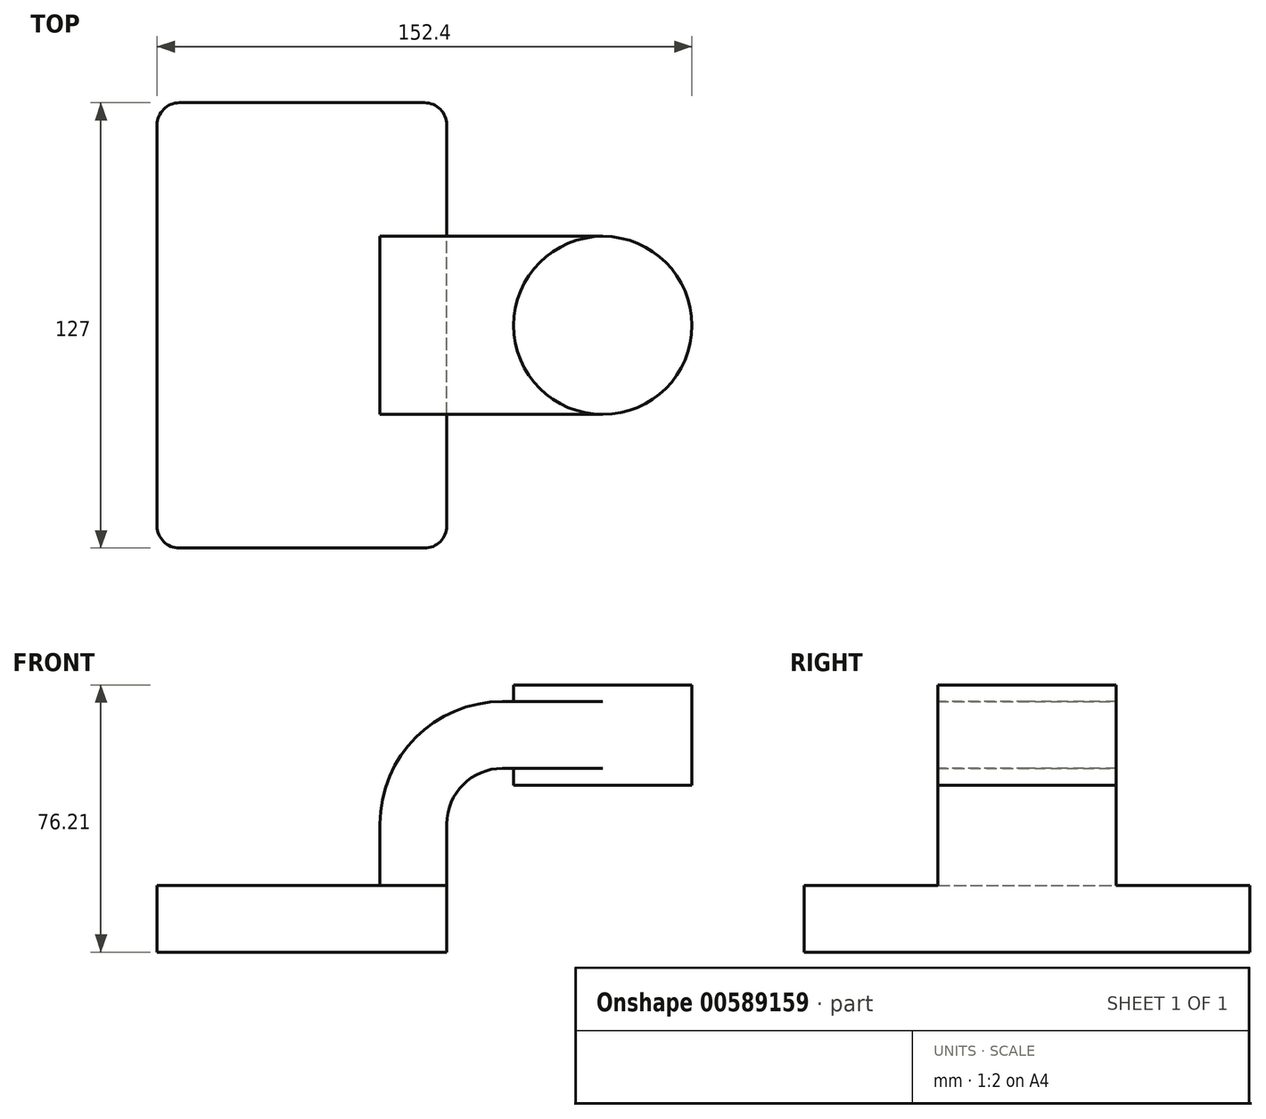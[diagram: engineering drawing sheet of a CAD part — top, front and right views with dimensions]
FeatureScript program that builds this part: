
annotation { "Feature Type Name" : "Feature", "Feature Type Description" : "" }
export const myFeature = defineFeature(function(context is Context, id is Id, definition is map)
    precondition{}
    {
        {
            var Q0;
            Q0=qCreatedBy(makeId("Front.planeOp"),FACE);
            var sketch = newSketch(context, id + "F0", { "sketchPlane" : qUnion([Q0])});
            skLineSegment(sketch, "E0.bottom", {"start": v(-41.28, -9.53) * mm, "end": v(41.28, -9.53) * mm});
            skLineSegment(sketch, "E0.top", {"start": v(-41.28, 9.53) * mm, "end": v(41.28, 9.53) * mm});
            skLineSegment(sketch, "E0.left", {"start": v(-41.28, -9.53) * mm, "end": v(-41.28, 9.53) * mm});
            skLineSegment(sketch, "E0.right", {"start": v(41.28, -9.53) * mm, "end": v(41.28, 9.53) * mm});
            skPoint(sketch, "E0.middle", {"position": v(0, 0) * mm});
            skLineSegment(sketch, "E1.bottom", {"start": v(60.33, 38.1) * mm, "end": v(111.13, 38.1) * mm});
            skLineSegment(sketch, "E1.top", {"start": v(60.33, 66.67) * mm, "end": v(111.13, 66.67) * mm});
            skLineSegment(sketch, "E1.left", {"start": v(60.33, 38.1) * mm, "end": v(60.33, 66.67) * mm});
            skLineSegment(sketch, "E1.right", {"start": v(111.13, 38.1) * mm, "end": v(111.13, 66.67) * mm});
            skPoint(sketch, "E1.middle", {"position": v(85.73, 52.39) * mm});
            skLineSegment(sketch, "E2", {"start": v(41.28, 9.53) * mm, "end": v(41.28, 27) * mm});
            skArc(sketch, "E3", {"start": v(41.27, 27) * mm, "mid": v(45.92, 38.23) * mm, "end": v(57.15, 42.88) * mm});
            skLineSegment(sketch, "E4", {"start": v(57.15, 42.88) * mm, "end": v(85.72, 42.88) * mm});
            skLineSegment(sketch, "E5.0", {"start": v(57.15, 61.93) * mm, "end": v(85.73, 61.93) * mm});
            skArc(sketch, "E5.1", {"start": v(22.23, 27) * mm, "mid": v(32.45, 51.7) * mm, "end": v(57.15, 61.93) * mm});
            skLineSegment(sketch, "E5.2", {"start": v(22.22, 9.53) * mm, "end": v(22.22, 27) * mm});
            skFitSpline(sketch, "E6", {"points": [v(-41.28, 9.53) * mm, v(57.15, 61.93) * mm], "startDerivative": vector(0, 93.05) * mm, "endDerivative": vector(146.16, 0) * mm});
            skPoint(sketch, "E7", {"position": v(85.73, 66.67) * mm});
            skLineSegment(sketch, "E8", {"start": v(85.73, 38.1) * mm, "end": v(85.73, 66.67) * mm});
            skSolve(sketch);
        }
        {
            var Q0;
            Q0=makeQuery(id+"F0.imprint","IMPRINT",FACE,{"disambiguationData":[TD([[makeQuery(id+"F0.imprint","IMPRINT",EDGE,{"derivedFrom":sQuery(id+"F0.wireOp",EDGE,"E0.bottom")}),1.0]])]});
            extrude(context, id + "F1", {"entities" : qUnion([Q0]), "endBound" : BoundingType.SYMMETRIC, "depth" : 127 * mm, "offsetDistance" : 25.4 * mm});
        }
        {
            var Q0;
            {var subQ0=sQuery(id+"F0.wireOp",EDGE,"E2");Q0=makeQuery(id+"F0.imprint","IMPRINT",FACE,{"disambiguationData":[TD([[makeQuery(id+"F0.imprint","IMPRINT",EDGE,{"derivedFrom":subQ0}),1.0]])]});}
            var Q1;
            {var subQ5=sQuery(id+"F0.wireOp",EDGE,"hNIXjnto-g6vo-ROrM-UPKH-p0qfGfHphnBU");Q1=makeQuery(id+"F0.imprint","IMPRINT",FACE,{"disambiguationData":[TD([[makeQuery(id+"F0.imprint","IMPRINT",EDGE,{"derivedFrom":subQ5}),-1.0]])]});}
            var Q2;
            {var subQ0=sQuery(id+"F0.wireOp",EDGE,"E4");var subQ1=sQuery(id+"F0.wireOp",EDGE,"E1.left");var subQ2=makeQuery(id+"F0.imprint","INTERSECT",VERTEX,{"derivedFrom":[subQ1,subQ0]});Q2=makeQuery(id+"F0.imprint","IMPRINT",FACE,{"disambiguationData":[TD([[makeQuery(id+"F0.imprint","IMPRINT",EDGE,{"disambiguationData":[TD([[subQ2,-1.0]])],"derivedFrom":subQ1}),-1.0]])]});}
            extrude(context, id + "F2", {"entities" : qUnion([Q0, Q1, Q2]), "operationType" : NewBodyOperationType.ADD, "endBound" : BoundingType.SYMMETRIC, "depth" : 50.8 * mm, "offsetDistance" : 25.4 * mm});
        }
        {
            var Q0;
            Q0=makeQuery(id+"F0.imprint","IMPRINT",FACE,{"disambiguationData":[TD([[makeQuery(id+"F0.imprint","IMPRINT",EDGE,{"derivedFrom":sQuery(id+"F0.wireOp",EDGE,"E5.1")}),1.0]])]});
            extrude(context, id + "F3", {"entities" : qUnion([Q0]), "operationType" : NewBodyOperationType.ADD, "endBound" : BoundingType.SYMMETRIC, "depth" : 15.88 * mm, "offsetDistance" : 25.4 * mm});
        }
        {
            var Q0;
            {var subQ4=sQuery(id+"F0.wireOp",EDGE,"E1.right");Q0=makeQuery(id+"F0.imprint","IMPRINT",FACE,{"disambiguationData":[TD([[makeQuery(id+"F0.imprint","IMPRINT",EDGE,{"derivedFrom":subQ4}),1.0]])]});}
            var Q1;
            Q1=sQuery(id+"F0.wireOp",EDGE,"E8");
            revolve(context, id + "F4", {"operationType" : NewBodyOperationType.ADD, "entities" : qUnion([Q0]), "axis" : qUnion([Q1]), "revolveType" : RevolveType.FULL});
        }
        {
            var Q0;
            Q0=makeQuery(id+"F1.opExtrude","CAP_EDGE",EDGE,{"disambiguationData":[OSD([sQuery(id+"F0.wireOp",EDGE,"E0.right")])],"isStart":false});
            var Q1;
            Q1=makeQuery(id+"F1.opExtrude","CAP_EDGE",EDGE,{"disambiguationData":[OSD([sQuery(id+"F0.wireOp",EDGE,"E0.left")])],"isStart":false});
            var Q2;
            Q2=makeQuery(id+"F1.opExtrude","CAP_EDGE",EDGE,{"disambiguationData":[OSD([sQuery(id+"F0.wireOp",EDGE,"E0.right")])],"isStart":true});
            var Q3;
            Q3=makeQuery(id+"F1.opExtrude","CAP_EDGE",EDGE,{"disambiguationData":[OSD([sQuery(id+"F0.wireOp",EDGE,"E0.left")])],"isStart":true});
            fillet(context, id + "F5", {"entities" : qUnion([Q0, Q1, Q2, Q3]), "radius" : 6.35 * mm, "tangentPropagation" : true, "allowEdgeOverflow" : false});
        }
    });
